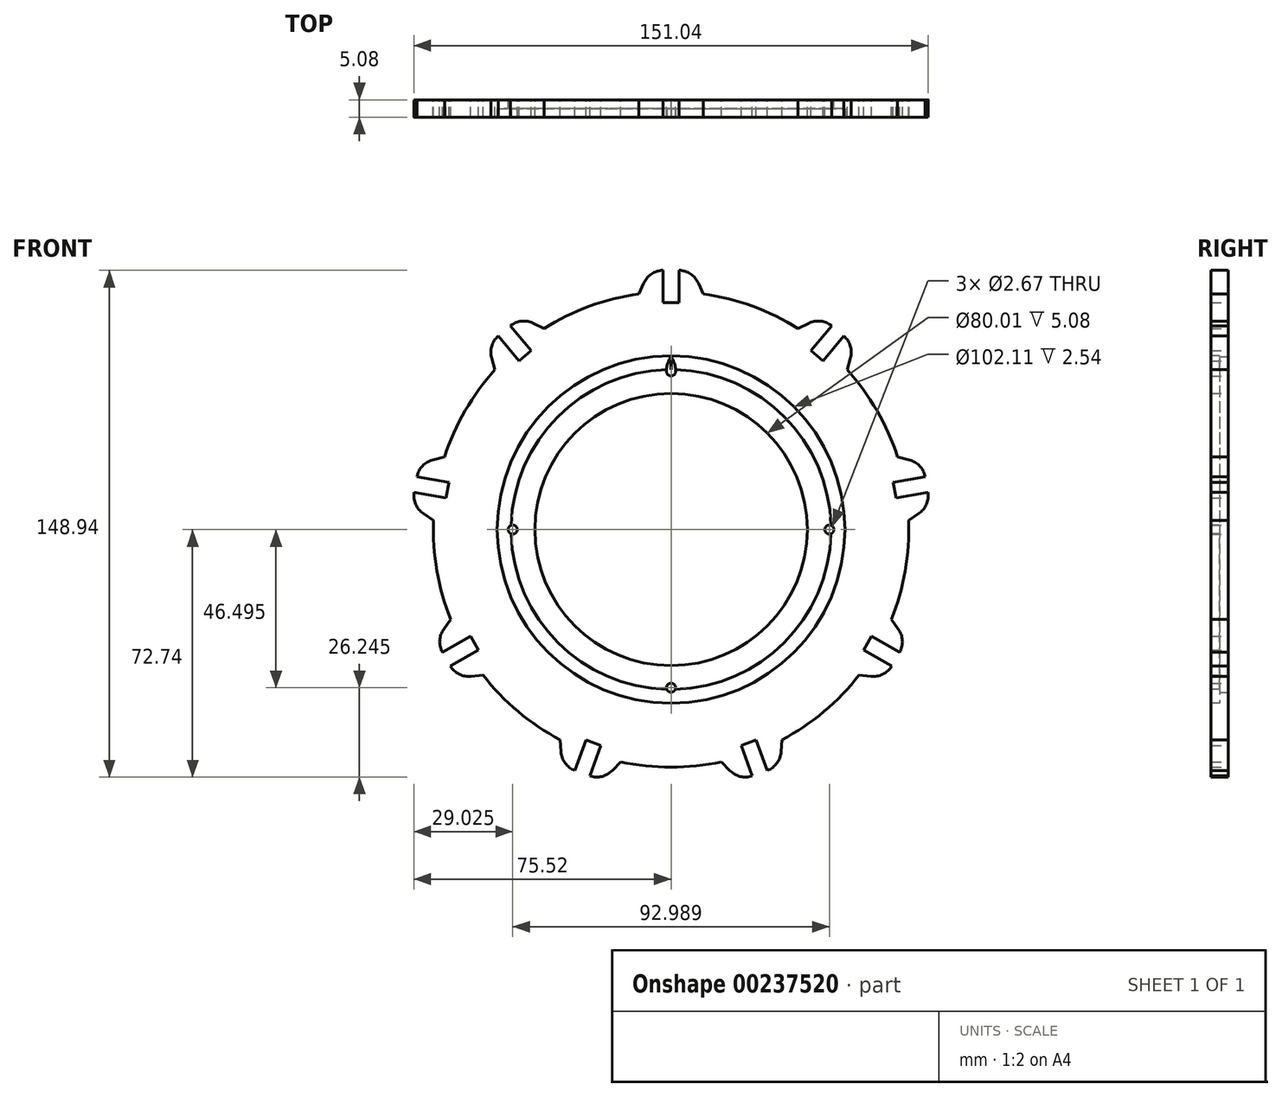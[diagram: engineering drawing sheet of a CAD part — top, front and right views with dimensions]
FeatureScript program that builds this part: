
annotation { "Feature Type Name" : "Feature", "Feature Type Description" : "" }
export const myFeature = defineFeature(function(context is Context, id is Id, definition is map)
    precondition{}
    {
        {
            var Q0;
            Q0=qCreatedBy(makeId("Front.planeOp"),FACE);
            var sketch = newSketch(context, id + "F0", { "sketchPlane" : qUnion([Q0])});
            skCircle(sketch, "E0", {"center": v(0, 0) * mm, "radius": 69.85 * mm});
            skCircle(sketch, "E1", {"center": v(0, 0) * mm, "radius": 40 * mm});
            skCircle(sketch, "E2", {"center": v(0, 0) * mm, "radius": 46.5 * mm, "construction": true});
            skPoint(sketch, "E3.center", {"position": v(0, -7.07) * mm});
            skLineSegment(sketch, "E4", {"start": v(-9.44, 69.2) * mm, "end": v(-8.02, 72.42) * mm});
            skLineSegment(sketch, "E5", {"start": v(-2.21, 76.2) * mm, "end": v(2.21, 76.2) * mm});
            skLineSegment(sketch, "E6", {"start": v(8.02, 72.42) * mm, "end": v(9.44, 69.2) * mm});
            skPoint(sketch, "E7", {"position": v(0, 76.2) * mm});
            skLineSegment(sketch, "E8", {"start": v(-9.44, 69.2) * mm, "end": v(-40, 0) * mm, "construction": true});
            skLineSegment(sketch, "E9", {"start": v(40, 0) * mm, "end": v(9.44, 69.2) * mm, "construction": true});
            skLineSegment(sketch, "E10", {"start": v(-2.35, 76.2) * mm, "end": v(-2.35, 66.67) * mm});
            skLineSegment(sketch, "E11", {"start": v(-2.35, 66.68) * mm, "end": v(2.35, 66.68) * mm});
            skLineSegment(sketch, "E12", {"start": v(2.35, 66.67) * mm, "end": v(2.35, 76.2) * mm});
            skPoint(sketch, "E13", {"position": v(0, 66.67) * mm});
            skPoint(sketch, "E14.visualSharp", {"position": v(-6.35, 76.2) * mm});
            skArc(sketch, "E14.filletArc", {"start": v(-2.21, 76.2) * mm, "mid": v(-5.68, 75.17) * mm, "end": v(-8.02, 72.42) * mm});
            skPoint(sketch, "E15.visualSharp", {"position": v(6.35, 76.2) * mm});
            skArc(sketch, "E15.filletArc", {"start": v(8.02, 72.42) * mm, "mid": v(5.68, 75.17) * mm, "end": v(2.21, 76.2) * mm});
            skCircle(sketch, "E16.MirrorC", {"center": v(0, 46.5) * mm, "radius": 1.33 * mm});
            skCircle(sketch, "E17", {"center": v(0, 0) * mm, "radius": 66.72 * mm, "construction": true});
            skCircle(sketch, "E18.1.0", {"center": v(-46.5, 0) * mm, "radius": 1.33 * mm});
            skCircle(sketch, "E18.2.0", {"center": v(0, -46.5) * mm, "radius": 1.33 * mm});
            skCircle(sketch, "E18.3.0", {"center": v(46.5, 0) * mm, "radius": 1.33 * mm});
            skCircle(sketch, "E19", {"center": v(0, 0) * mm, "radius": 50.8 * mm, "construction": true});
            skArc(sketch, "E20", {"start": v(1.33, 46.48) * mm, "mid": v(1, 48.74) * mm, "end": v(0, 50.8) * mm});
            skArc(sketch, "E21", {"start": v(0, 50.8) * mm, "mid": v(-1, 48.74) * mm, "end": v(-1.33, 46.48) * mm});
            skLineSegment(sketch, "E22.1.0", {"start": v(-51.72, 46.95) * mm, "end": v(-52.7, 50.32) * mm});
            skArc(sketch, "E22.1.1", {"start": v(-50.68, 56.95) * mm, "mid": v(-52.67, 53.93) * mm, "end": v(-52.7, 50.32) * mm});
            skLineSegment(sketch, "E22.1.2", {"start": v(-50.78, 56.86) * mm, "end": v(-44.66, 49.57) * mm});
            skLineSegment(sketch, "E22.1.3", {"start": v(-41.06, 52.59) * mm, "end": v(-47.18, 59.88) * mm});
            skArc(sketch, "E22.1.4", {"start": v(-40.4, 60.63) * mm, "mid": v(-43.97, 61.23) * mm, "end": v(-47.29, 59.8) * mm});
            skLineSegment(sketch, "E22.1.5", {"start": v(-40.4, 60.63) * mm, "end": v(-37.26, 59.08) * mm});
            skLineSegment(sketch, "E22.1.6", {"start": v(-44.66, 49.57) * mm, "end": v(-41.06, 52.59) * mm});
            skLineSegment(sketch, "E22.2.0", {"start": v(-69.8, 2.72) * mm, "end": v(-72.7, 4.68) * mm});
            skArc(sketch, "E22.2.1", {"start": v(-75.43, 11.05) * mm, "mid": v(-75.01, 7.46) * mm, "end": v(-72.7, 4.68) * mm});
            skLineSegment(sketch, "E22.2.2", {"start": v(-75.45, 10.92) * mm, "end": v(-66.07, 9.26) * mm});
            skLineSegment(sketch, "E22.2.3", {"start": v(-65.25, 13.9) * mm, "end": v(-74.63, 15.55) * mm});
            skArc(sketch, "E22.2.4", {"start": v(-69.92, 20.47) * mm, "mid": v(-73.04, 18.65) * mm, "end": v(-74.66, 15.41) * mm});
            skLineSegment(sketch, "E22.2.5", {"start": v(-69.92, 20.47) * mm, "end": v(-66.52, 21.31) * mm});
            skLineSegment(sketch, "E22.2.6", {"start": v(-66.07, 9.26) * mm, "end": v(-65.25, 13.9) * mm});
            skLineSegment(sketch, "E22.3.0", {"start": v(-55.22, -42.78) * mm, "end": v(-58.7, -43.15) * mm});
            skArc(sketch, "E22.3.1", {"start": v(-64.88, -40.02) * mm, "mid": v(-62.26, -42.5) * mm, "end": v(-58.7, -43.15) * mm});
            skLineSegment(sketch, "E22.3.2", {"start": v(-64.82, -40.13) * mm, "end": v(-56.57, -35.37) * mm});
            skLineSegment(sketch, "E22.3.3", {"start": v(-58.92, -31.3) * mm, "end": v(-67.17, -36.07) * mm});
            skArc(sketch, "E22.3.4", {"start": v(-66.72, -29.26) * mm, "mid": v(-67.94, -32.67) * mm, "end": v(-67.1, -36.18) * mm});
            skLineSegment(sketch, "E22.3.5", {"start": v(-66.72, -29.26) * mm, "end": v(-64.66, -26.43) * mm});
            skLineSegment(sketch, "E22.3.6", {"start": v(-56.57, -35.37) * mm, "end": v(-58.92, -31.3) * mm});
            skLineSegment(sketch, "E22.4.0", {"start": v(-14.8, -68.26) * mm, "end": v(-17.23, -70.8) * mm});
            skArc(sketch, "E22.4.1", {"start": v(-23.98, -72.36) * mm, "mid": v(-20.37, -72.58) * mm, "end": v(-17.23, -70.8) * mm});
            skLineSegment(sketch, "E22.4.2", {"start": v(-23.85, -72.4) * mm, "end": v(-20.6, -63.46) * mm});
            skLineSegment(sketch, "E22.4.3", {"start": v(-25.01, -61.85) * mm, "end": v(-28.27, -70.8) * mm});
            skArc(sketch, "E22.4.4", {"start": v(-32.3, -65.3) * mm, "mid": v(-31.05, -68.7) * mm, "end": v(-28.14, -70.85) * mm});
            skLineSegment(sketch, "E22.4.5", {"start": v(-32.3, -65.3) * mm, "end": v(-32.54, -61.8) * mm});
            skLineSegment(sketch, "E22.4.6", {"start": v(-20.6, -63.46) * mm, "end": v(-25.01, -61.85) * mm});
            skLineSegment(sketch, "E22.5.0", {"start": v(32.54, -61.8) * mm, "end": v(32.3, -65.3) * mm});
            skArc(sketch, "E22.5.1", {"start": v(28.14, -70.85) * mm, "mid": v(31.05, -68.7) * mm, "end": v(32.3, -65.3) * mm});
            skLineSegment(sketch, "E22.5.2", {"start": v(28.27, -70.8) * mm, "end": v(25.01, -61.85) * mm});
            skLineSegment(sketch, "E22.5.3", {"start": v(20.6, -63.46) * mm, "end": v(23.85, -72.4) * mm});
            skArc(sketch, "E22.5.4", {"start": v(17.23, -70.8) * mm, "mid": v(20.37, -72.58) * mm, "end": v(23.98, -72.36) * mm});
            skLineSegment(sketch, "E22.5.5", {"start": v(17.23, -70.8) * mm, "end": v(14.8, -68.26) * mm});
            skLineSegment(sketch, "E22.5.6", {"start": v(25.01, -61.85) * mm, "end": v(20.6, -63.46) * mm});
            skLineSegment(sketch, "E22.6.0", {"start": v(64.66, -26.43) * mm, "end": v(66.72, -29.26) * mm});
            skArc(sketch, "E22.6.1", {"start": v(67.1, -36.18) * mm, "mid": v(67.94, -32.67) * mm, "end": v(66.72, -29.26) * mm});
            skLineSegment(sketch, "E22.6.2", {"start": v(67.17, -36.07) * mm, "end": v(58.92, -31.3) * mm});
            skLineSegment(sketch, "E22.6.3", {"start": v(56.57, -35.37) * mm, "end": v(64.82, -40.13) * mm});
            skArc(sketch, "E22.6.4", {"start": v(58.7, -43.15) * mm, "mid": v(62.26, -42.5) * mm, "end": v(64.88, -40.02) * mm});
            skLineSegment(sketch, "E22.6.5", {"start": v(58.7, -43.15) * mm, "end": v(55.22, -42.78) * mm});
            skLineSegment(sketch, "E22.6.6", {"start": v(58.92, -31.3) * mm, "end": v(56.57, -35.37) * mm});
            skLineSegment(sketch, "E22.7.0", {"start": v(66.52, 21.31) * mm, "end": v(69.92, 20.47) * mm});
            skArc(sketch, "E22.7.1", {"start": v(74.66, 15.41) * mm, "mid": v(73.04, 18.65) * mm, "end": v(69.92, 20.47) * mm});
            skLineSegment(sketch, "E22.7.2", {"start": v(74.63, 15.55) * mm, "end": v(65.25, 13.9) * mm});
            skLineSegment(sketch, "E22.7.3", {"start": v(66.07, 9.26) * mm, "end": v(75.45, 10.92) * mm});
            skArc(sketch, "E22.7.4", {"start": v(72.7, 4.68) * mm, "mid": v(75.01, 7.46) * mm, "end": v(75.43, 11.05) * mm});
            skLineSegment(sketch, "E22.7.5", {"start": v(72.7, 4.68) * mm, "end": v(69.8, 2.72) * mm});
            skLineSegment(sketch, "E22.7.6", {"start": v(65.25, 13.9) * mm, "end": v(66.07, 9.26) * mm});
            skLineSegment(sketch, "E22.8.0", {"start": v(37.26, 59.08) * mm, "end": v(40.4, 60.63) * mm});
            skArc(sketch, "E22.8.1", {"start": v(47.29, 59.8) * mm, "mid": v(43.97, 61.23) * mm, "end": v(40.4, 60.63) * mm});
            skLineSegment(sketch, "E22.8.2", {"start": v(47.18, 59.88) * mm, "end": v(41.06, 52.59) * mm});
            skLineSegment(sketch, "E22.8.3", {"start": v(44.66, 49.57) * mm, "end": v(50.78, 56.86) * mm});
            skArc(sketch, "E22.8.4", {"start": v(52.7, 50.32) * mm, "mid": v(52.67, 53.93) * mm, "end": v(50.68, 56.95) * mm});
            skLineSegment(sketch, "E22.8.5", {"start": v(52.7, 50.32) * mm, "end": v(51.72, 46.95) * mm});
            skLineSegment(sketch, "E22.8.6", {"start": v(41.06, 52.59) * mm, "end": v(44.66, 49.57) * mm});
            skSolve(sketch);
        }
        {
            var Q0;
            Q0=makeQuery(id+"F0.imprint","IMPRINT",FACE,{"disambiguationData":[TD([[makeQuery(id+"F0.imprint","IMPRINT",EDGE,{"derivedFrom":sQuery(id+"F0.wireOp",EDGE,"E1")}),-1.0]])]});
            var Q1;
            {var subQ0=sQuery(id+"F0.wireOp",EDGE,"E22.1.5");Q1=makeQuery(id+"F0.imprint","IMPRINT",FACE,{"disambiguationData":[TD([[makeQuery(id+"F0.imprint","IMPRINT",EDGE,{"derivedFrom":subQ0}),-1.0]])]});}
            var Q2;
            {var subQ0=sQuery(id+"F0.wireOp",EDGE,"E22.1.0");Q2=makeQuery(id+"F0.imprint","IMPRINT",FACE,{"disambiguationData":[TD([[makeQuery(id+"F0.imprint","IMPRINT",EDGE,{"derivedFrom":subQ0}),-1.0]])]});}
            var Q3;
            {var subQ0=sQuery(id+"F0.wireOp",EDGE,"E4");Q3=makeQuery(id+"F0.imprint","IMPRINT",FACE,{"disambiguationData":[TD([[makeQuery(id+"F0.imprint","IMPRINT",EDGE,{"derivedFrom":subQ0}),-1.0]])]});}
            var Q4;
            {var subQ0=sQuery(id+"F0.wireOp",EDGE,"E6");Q4=makeQuery(id+"F0.imprint","IMPRINT",FACE,{"disambiguationData":[TD([[makeQuery(id+"F0.imprint","IMPRINT",EDGE,{"derivedFrom":subQ0}),-1.0]])]});}
            var Q5;
            {var subQ0=sQuery(id+"F0.wireOp",EDGE,"E22.8.0");Q5=makeQuery(id+"F0.imprint","IMPRINT",FACE,{"disambiguationData":[TD([[makeQuery(id+"F0.imprint","IMPRINT",EDGE,{"derivedFrom":subQ0}),-1.0]])]});}
            var Q6;
            {var subQ0=sQuery(id+"F0.wireOp",EDGE,"E22.8.5");Q6=makeQuery(id+"F0.imprint","IMPRINT",FACE,{"disambiguationData":[TD([[makeQuery(id+"F0.imprint","IMPRINT",EDGE,{"derivedFrom":subQ0}),-1.0]])]});}
            var Q7;
            {var subQ0=sQuery(id+"F0.wireOp",EDGE,"E22.7.0");Q7=makeQuery(id+"F0.imprint","IMPRINT",FACE,{"disambiguationData":[TD([[makeQuery(id+"F0.imprint","IMPRINT",EDGE,{"derivedFrom":subQ0}),-1.0]])]});}
            var Q8;
            {var subQ0=sQuery(id+"F0.wireOp",EDGE,"E22.7.5");Q8=makeQuery(id+"F0.imprint","IMPRINT",FACE,{"disambiguationData":[TD([[makeQuery(id+"F0.imprint","IMPRINT",EDGE,{"derivedFrom":subQ0}),-1.0]])]});}
            var Q9;
            {var subQ0=sQuery(id+"F0.wireOp",EDGE,"E22.6.0");Q9=makeQuery(id+"F0.imprint","IMPRINT",FACE,{"disambiguationData":[TD([[makeQuery(id+"F0.imprint","IMPRINT",EDGE,{"derivedFrom":subQ0}),-1.0]])]});}
            var Q10;
            {var subQ0=sQuery(id+"F0.wireOp",EDGE,"E22.6.5");Q10=makeQuery(id+"F0.imprint","IMPRINT",FACE,{"disambiguationData":[TD([[makeQuery(id+"F0.imprint","IMPRINT",EDGE,{"derivedFrom":subQ0}),-1.0]])]});}
            var Q11;
            {var subQ0=sQuery(id+"F0.wireOp",EDGE,"E22.5.5");Q11=makeQuery(id+"F0.imprint","IMPRINT",FACE,{"disambiguationData":[TD([[makeQuery(id+"F0.imprint","IMPRINT",EDGE,{"derivedFrom":subQ0}),-1.0]])]});}
            var Q12;
            {var subQ0=sQuery(id+"F0.wireOp",EDGE,"E22.5.0");Q12=makeQuery(id+"F0.imprint","IMPRINT",FACE,{"disambiguationData":[TD([[makeQuery(id+"F0.imprint","IMPRINT",EDGE,{"derivedFrom":subQ0}),-1.0]])]});}
            var Q13;
            {var subQ0=sQuery(id+"F0.wireOp",EDGE,"E22.4.5");Q13=makeQuery(id+"F0.imprint","IMPRINT",FACE,{"disambiguationData":[TD([[makeQuery(id+"F0.imprint","IMPRINT",EDGE,{"derivedFrom":subQ0}),-1.0]])]});}
            var Q14;
            {var subQ0=sQuery(id+"F0.wireOp",EDGE,"E22.4.0");Q14=makeQuery(id+"F0.imprint","IMPRINT",FACE,{"disambiguationData":[TD([[makeQuery(id+"F0.imprint","IMPRINT",EDGE,{"derivedFrom":subQ0}),-1.0]])]});}
            var Q15;
            {var subQ0=sQuery(id+"F0.wireOp",EDGE,"E22.3.0");Q15=makeQuery(id+"F0.imprint","IMPRINT",FACE,{"disambiguationData":[TD([[makeQuery(id+"F0.imprint","IMPRINT",EDGE,{"derivedFrom":subQ0}),-1.0]])]});}
            var Q16;
            {var subQ0=sQuery(id+"F0.wireOp",EDGE,"E22.3.5");Q16=makeQuery(id+"F0.imprint","IMPRINT",FACE,{"disambiguationData":[TD([[makeQuery(id+"F0.imprint","IMPRINT",EDGE,{"derivedFrom":subQ0}),-1.0]])]});}
            var Q17;
            {var subQ0=sQuery(id+"F0.wireOp",EDGE,"E22.2.0");Q17=makeQuery(id+"F0.imprint","IMPRINT",FACE,{"disambiguationData":[TD([[makeQuery(id+"F0.imprint","IMPRINT",EDGE,{"derivedFrom":subQ0}),-1.0]])]});}
            var Q18;
            {var subQ0=sQuery(id+"F0.wireOp",EDGE,"E22.2.5");Q18=makeQuery(id+"F0.imprint","IMPRINT",FACE,{"disambiguationData":[TD([[makeQuery(id+"F0.imprint","IMPRINT",EDGE,{"derivedFrom":subQ0}),-1.0]])]});}
            extrude(context, id + "F1", {"entities" : qUnion([Q0, Q1, Q2, Q3, Q4, Q5, Q6, Q7, Q8, Q9, Q10, Q11, Q12, Q13, Q14, Q15, Q16, Q17, Q18]), "depth" : 5.08 * mm});
        }
        {
            var Q0;
            Q0=makeQuery(id+"F1.opExtrude","CAP_FACE",FACE,{"disambiguationData":[OSD([sQuery(id+"F0.wireOp",EDGE,"E0"),sQuery(id+"F0.wireOp",EDGE,"E1"),sQuery(id+"F0.wireOp",EDGE,"s7rXqqL2-3z2l-88EV-UIsY-hwb08Po9ZJjJ"),sQuery(id+"F0.wireOp",EDGE,"E3.1.0"),sQuery(id+"F0.wireOp",EDGE,"E3.2.0"),sQuery(id+"F0.wireOp",EDGE,"E3.3.0"),sQuery(id+"F0.wireOp",EDGE,"E4"),sQuery(id+"F0.wireOp",EDGE,"E6"),sQuery(id+"F0.wireOp",EDGE,"E10"),sQuery(id+"F0.wireOp",EDGE,"E11"),sQuery(id+"F0.wireOp",EDGE,"E12"),sQuery(id+"F0.wireOp",EDGE,"E14.filletArc"),sQuery(id+"F0.wireOp",EDGE,"E15.filletArc"),sQuery(id+"F0.wireOp",EDGE,"e3144966-756d-47fd-8283-5f46bd2110e0.1.0"),sQuery(id+"F0.wireOp",EDGE,"e3144966-756d-47fd-8283-5f46bd2110e0.1.1"),sQuery(id+"F0.wireOp",EDGE,"e3144966-756d-47fd-8283-5f46bd2110e0.1.2"),sQuery(id+"F0.wireOp",EDGE,"e3144966-756d-47fd-8283-5f46bd2110e0.1.3"),sQuery(id+"F0.wireOp",EDGE,"e3144966-756d-47fd-8283-5f46bd2110e0.1.4"),sQuery(id+"F0.wireOp",EDGE,"e3144966-756d-47fd-8283-5f46bd2110e0.1.6"),sQuery(id+"F0.wireOp",EDGE,"e3144966-756d-47fd-8283-5f46bd2110e0.1.7"),sQuery(id+"F0.wireOp",EDGE,"e3144966-756d-47fd-8283-5f46bd2110e0.2.0"),sQuery(id+"F0.wireOp",EDGE,"e3144966-756d-47fd-8283-5f46bd2110e0.2.1"),sQuery(id+"F0.wireOp",EDGE,"e3144966-756d-47fd-8283-5f46bd2110e0.2.2"),sQuery(id+"F0.wireOp",EDGE,"e3144966-756d-47fd-8283-5f46bd2110e0.2.3"),sQuery(id+"F0.wireOp",EDGE,"e3144966-756d-47fd-8283-5f46bd2110e0.2.4"),sQuery(id+"F0.wireOp",EDGE,"e3144966-756d-47fd-8283-5f46bd2110e0.2.6"),sQuery(id+"F0.wireOp",EDGE,"e3144966-756d-47fd-8283-5f46bd2110e0.2.7"),sQuery(id+"F0.wireOp",EDGE,"e3144966-756d-47fd-8283-5f46bd2110e0.3.0"),sQuery(id+"F0.wireOp",EDGE,"e3144966-756d-47fd-8283-5f46bd2110e0.3.1"),sQuery(id+"F0.wireOp",EDGE,"e3144966-756d-47fd-8283-5f46bd2110e0.3.2"),sQuery(id+"F0.wireOp",EDGE,"e3144966-756d-47fd-8283-5f46bd2110e0.3.3"),sQuery(id+"F0.wireOp",EDGE,"e3144966-756d-47fd-8283-5f46bd2110e0.3.4"),sQuery(id+"F0.wireOp",EDGE,"e3144966-756d-47fd-8283-5f46bd2110e0.3.6"),sQuery(id+"F0.wireOp",EDGE,"e3144966-756d-47fd-8283-5f46bd2110e0.3.7"),sQuery(id+"F0.wireOp",EDGE,"e3144966-756d-47fd-8283-5f46bd2110e0.4.0"),sQuery(id+"F0.wireOp",EDGE,"e3144966-756d-47fd-8283-5f46bd2110e0.4.1"),sQuery(id+"F0.wireOp",EDGE,"e3144966-756d-47fd-8283-5f46bd2110e0.4.2"),sQuery(id+"F0.wireOp",EDGE,"e3144966-756d-47fd-8283-5f46bd2110e0.4.3"),sQuery(id+"F0.wireOp",EDGE,"e3144966-756d-47fd-8283-5f46bd2110e0.4.4"),sQuery(id+"F0.wireOp",EDGE,"e3144966-756d-47fd-8283-5f46bd2110e0.4.6"),sQuery(id+"F0.wireOp",EDGE,"e3144966-756d-47fd-8283-5f46bd2110e0.4.7"),sQuery(id+"F0.wireOp",EDGE,"e3144966-756d-47fd-8283-5f46bd2110e0.5.0"),sQuery(id+"F0.wireOp",EDGE,"e3144966-756d-47fd-8283-5f46bd2110e0.5.1"),sQuery(id+"F0.wireOp",EDGE,"e3144966-756d-47fd-8283-5f46bd2110e0.5.2"),sQuery(id+"F0.wireOp",EDGE,"e3144966-756d-47fd-8283-5f46bd2110e0.5.3"),sQuery(id+"F0.wireOp",EDGE,"e3144966-756d-47fd-8283-5f46bd2110e0.5.4"),sQuery(id+"F0.wireOp",EDGE,"e3144966-756d-47fd-8283-5f46bd2110e0.5.6"),sQuery(id+"F0.wireOp",EDGE,"e3144966-756d-47fd-8283-5f46bd2110e0.5.7"),sQuery(id+"F0.wireOp",EDGE,"e3144966-756d-47fd-8283-5f46bd2110e0.6.0"),sQuery(id+"F0.wireOp",EDGE,"e3144966-756d-47fd-8283-5f46bd2110e0.6.1"),sQuery(id+"F0.wireOp",EDGE,"e3144966-756d-47fd-8283-5f46bd2110e0.6.2"),sQuery(id+"F0.wireOp",EDGE,"e3144966-756d-47fd-8283-5f46bd2110e0.6.3"),sQuery(id+"F0.wireOp",EDGE,"e3144966-756d-47fd-8283-5f46bd2110e0.6.4"),sQuery(id+"F0.wireOp",EDGE,"e3144966-756d-47fd-8283-5f46bd2110e0.6.6"),sQuery(id+"F0.wireOp",EDGE,"e3144966-756d-47fd-8283-5f46bd2110e0.6.7"),sQuery(id+"F0.wireOp",EDGE,"e3144966-756d-47fd-8283-5f46bd2110e0.7.0"),sQuery(id+"F0.wireOp",EDGE,"e3144966-756d-47fd-8283-5f46bd2110e0.7.1"),sQuery(id+"F0.wireOp",EDGE,"e3144966-756d-47fd-8283-5f46bd2110e0.7.2"),sQuery(id+"F0.wireOp",EDGE,"e3144966-756d-47fd-8283-5f46bd2110e0.7.3"),sQuery(id+"F0.wireOp",EDGE,"e3144966-756d-47fd-8283-5f46bd2110e0.7.4"),sQuery(id+"F0.wireOp",EDGE,"e3144966-756d-47fd-8283-5f46bd2110e0.7.6"),sQuery(id+"F0.wireOp",EDGE,"e3144966-756d-47fd-8283-5f46bd2110e0.7.7"),sQuery(id+"F0.wireOp",EDGE,"e3144966-756d-47fd-8283-5f46bd2110e0.8.0"),sQuery(id+"F0.wireOp",EDGE,"e3144966-756d-47fd-8283-5f46bd2110e0.8.1"),sQuery(id+"F0.wireOp",EDGE,"e3144966-756d-47fd-8283-5f46bd2110e0.8.2"),sQuery(id+"F0.wireOp",EDGE,"e3144966-756d-47fd-8283-5f46bd2110e0.8.3"),sQuery(id+"F0.wireOp",EDGE,"e3144966-756d-47fd-8283-5f46bd2110e0.8.4"),sQuery(id+"F0.wireOp",EDGE,"e3144966-756d-47fd-8283-5f46bd2110e0.8.6"),sQuery(id+"F0.wireOp",EDGE,"e3144966-756d-47fd-8283-5f46bd2110e0.8.7")])],"isStart":false});
            var sketch = newSketch(context, id + "F2", { "sketchPlane" : qUnion([Q0])});
            skCircle(sketch, "E23", {"center": v(0, 0) * mm, "radius": 47 * mm});
            skCircle(sketch, "E24", {"center": v(0, 0) * mm, "radius": 51.05 * mm});
            skSolve(sketch);
        }
        {
            var Q0;
            Q0=makeQuery(id+"F2.imprint","IMPRINT",FACE,{"disambiguationData":[TD([[makeQuery(id+"F2.imprint","IMPRINT",EDGE,{"derivedFrom":sQuery(id+"F2.wireOp",EDGE,"E24")}),1.0]])]});
            var Q1;
            {var subQ0=sQuery(id+"F2.wireOp",EDGE,"E23");var subQ12=makeQuery(id+"F1.opExtrude","CAP_EDGE",EDGE,{"disambiguationData":[OSD([sQuery(id+"F0.wireOp",EDGE,"E20")])],"isStart":false});var subQ15=makeQuery(id+"F2.imprint","INTERSECT",VERTEX,{"derivedFrom":[subQ12,subQ0]});Q1=makeQuery(id+"F2.imprint","IMPRINT",FACE,{"disambiguationData":[TD([[makeQuery(id+"F2.imprint","IMPRINT",EDGE,{"disambiguationData":[TD([[subQ15,1.0]])],"derivedFrom":subQ0}),-1.0]])]});}
            extrude(context, id + "F3", {"entities" : qUnion([Q0, Q1]), "operationType" : NewBodyOperationType.REMOVE, "oppositeDirection" : true, "depth" : 2.54 * mm});
        }
        {
            var Q0;
            {var subQ0=sQuery(id+"F0.wireOp",EDGE,"E22.4.5");var subQ1=sQuery(id+"F0.wireOp",EDGE,"E22.3.6");var subQ2=sQuery(id+"F0.wireOp",EDGE,"E22.3.4");var subQ3=sQuery(id+"F0.wireOp",EDGE,"E22.4.2");var subQ4=sQuery(id+"F0.wireOp",EDGE,"E22.3.2");var subQ5=sQuery(id+"F0.wireOp",EDGE,"E22.4.4");var subQ6=sQuery(id+"F0.wireOp",EDGE,"E22.3.3");var subQ7=sQuery(id+"F0.wireOp",EDGE,"E22.3.1");var subQ8=sQuery(id+"F0.wireOp",EDGE,"E22.4.0");var subQ9=sQuery(id+"F0.wireOp",EDGE,"E22.2.6");var subQ10=sQuery(id+"F0.wireOp",EDGE,"E22.2.4");var subQ11=sQuery(id+"F0.wireOp",EDGE,"E22.2.2");var subQ12=sQuery(id+"F0.wireOp",EDGE,"E22.2.0");var subQ13=sQuery(id+"F0.wireOp",EDGE,"E22.1.2");var subQ14=sQuery(id+"F0.wireOp",EDGE,"E22.1.6");var subQ15=sQuery(id+"F0.wireOp",EDGE,"E22.5.0");var subQ16=sQuery(id+"F0.wireOp",EDGE,"E0");var subQ17=sQuery(id+"F0.wireOp",EDGE,"E22.6.5");var subQ18=sQuery(id+"F0.wireOp",EDGE,"E22.6.1");var subQ19=sQuery(id+"F0.wireOp",EDGE,"E12");var subQ20=sQuery(id+"F0.wireOp",EDGE,"E22.5.5");var subQ21=sQuery(id+"F0.wireOp",EDGE,"E22.3.0");var subQ22=sQuery(id+"F0.wireOp",EDGE,"E22.7.5");var subQ23=sQuery(id+"F0.wireOp",EDGE,"E22.3.5");var subQ24=sQuery(id+"F0.wireOp",EDGE,"E22.4.3");var subQ25=sQuery(id+"F0.wireOp",EDGE,"E22.8.5");var subQ26=sQuery(id+"F0.wireOp",EDGE,"E22.7.0");var subQ27=sQuery(id+"F0.wireOp",EDGE,"E22.1.1");var subQ28=sQuery(id+"F0.wireOp",EDGE,"E22.8.4");var subQ29=sQuery(id+"F0.wireOp",EDGE,"E14.filletArc");var subQ30=sQuery(id+"F0.wireOp",EDGE,"E22.6.0");var subQ31=sQuery(id+"F0.wireOp",EDGE,"E22.1.3");var subQ32=sQuery(id+"F0.wireOp",EDGE,"E22.8.6");var subQ33=sQuery(id+"F0.wireOp",EDGE,"E6");var subQ34=sQuery(id+"F0.wireOp",EDGE,"E22.8.0");var subQ35=sQuery(id+"F0.wireOp",EDGE,"E22.7.1");var subQ36=sQuery(id+"F0.wireOp",EDGE,"E4");var subQ37=sQuery(id+"F0.wireOp",EDGE,"E22.1.5");var subQ38=sQuery(id+"F0.wireOp",EDGE,"E22.6.4");var subQ39=sQuery(id+"F0.wireOp",EDGE,"E22.5.1");var subQ40=sQuery(id+"F0.wireOp",EDGE,"E22.4.6");var subQ41=sQuery(id+"F0.wireOp",EDGE,"E22.1.0");var subQ42=sQuery(id+"F0.wireOp",EDGE,"E22.2.5");var subQ43=sQuery(id+"F0.wireOp",EDGE,"E10");var subQ44=sQuery(id+"F0.wireOp",EDGE,"E22.6.6");var subQ45=sQuery(id+"F0.wireOp",EDGE,"E11");var subQ46=sQuery(id+"F0.wireOp",EDGE,"E15.filletArc");var subQ47=sQuery(id+"F0.wireOp",EDGE,"E22.2.3");var subQ48=sQuery(id+"F0.wireOp",EDGE,"E22.2.1");var subQ49=sQuery(id+"F0.wireOp",EDGE,"E22.4.1");var subQ50=sQuery(id+"F0.wireOp",EDGE,"E22.1.4");var subQ51=sQuery(id+"F0.wireOp",EDGE,"E22.5.2");var subQ52=sQuery(id+"F0.wireOp",EDGE,"E22.8.3");var subQ53=sQuery(id+"F0.wireOp",EDGE,"E22.5.3");var subQ54=sQuery(id+"F0.wireOp",EDGE,"E22.5.4");var subQ55=sQuery(id+"F0.wireOp",EDGE,"E22.5.6");var subQ56=sQuery(id+"F0.wireOp",EDGE,"E22.6.2");var subQ57=sQuery(id+"F0.wireOp",EDGE,"E22.6.3");var subQ58=sQuery(id+"F0.wireOp",EDGE,"E22.7.2");var subQ59=sQuery(id+"F0.wireOp",EDGE,"E22.7.3");var subQ60=sQuery(id+"F0.wireOp",EDGE,"E22.7.4");var subQ61=sQuery(id+"F0.wireOp",EDGE,"E22.7.6");var subQ62=sQuery(id+"F0.wireOp",EDGE,"E22.8.1");var subQ63=sQuery(id+"F0.wireOp",EDGE,"E22.8.2");Q0=makeQuery(id+"F3.boolean.opBoolean","SPLIT",FACE,{"disambiguationData":[TD([makeQuery(id+"F1.opExtrude","SWEPT_FACE",FACE,{"disambiguationData":[OSD([subQ36])]})])],"derivedFrom":makeQuery(id+"F1.opExtrude","CAP_FACE",FACE,{"disambiguationData":[OSD([subQ16,sQuery(id+"F0.wireOp",EDGE,"E1"),subQ36,subQ33,subQ43,subQ45,subQ19,subQ29,subQ46,sQuery(id+"F0.wireOp",EDGE,"E16.MirrorC"),sQuery(id+"F0.wireOp",EDGE,"E18.1.0"),sQuery(id+"F0.wireOp",EDGE,"E18.2.0"),sQuery(id+"F0.wireOp",EDGE,"E18.3.0"),sQuery(id+"F0.wireOp",EDGE,"E20"),sQuery(id+"F0.wireOp",EDGE,"E21"),subQ41,subQ27,subQ13,subQ31,subQ50,subQ37,subQ14,subQ12,subQ48,subQ11,subQ47,subQ10,subQ42,subQ9,subQ21,subQ7,subQ4,subQ6,subQ2,subQ23,subQ1,subQ8,subQ49,subQ3,subQ24,subQ5,subQ0,subQ40,subQ15,subQ39,subQ51,subQ53,subQ54,subQ20,subQ55,subQ30,subQ18,subQ56,subQ57,subQ38,subQ17,subQ44,subQ26,subQ35,subQ58,subQ59,subQ60,subQ22,subQ61,subQ34,subQ62,subQ63,subQ52,subQ28,subQ25,subQ32])],"isStart":false})});}
            var sketch = newSketch(context, id + "F4", { "sketchPlane" : qUnion([Q0])});
            skLineSegment(sketch, "E25", {"start": v(-0.03, 51.05) * mm, "end": v(-0.03, 46.99) * mm});
            skLineSegment(sketch, "E26", {"start": v(0.03, 51.05) * mm, "end": v(0.03, 46.99) * mm});
            skLineSegment(sketch, "E27", {"start": v(-0.03, 49.02) * mm, "end": v(0.03, 49.02) * mm, "construction": true});
            skPoint(sketch, "E28", {"position": v(0, 49.02) * mm});
            skArc(sketch, "E29", {"start": v(0.03, 51.05) * mm, "mid": v(0, 51.05) * mm, "end": v(-0.03, 51.05) * mm});
            skArc(sketch, "E30", {"start": v(0.03, 46.99) * mm, "mid": v(0, 46.99) * mm, "end": v(-0.03, 46.99) * mm});
            skSolve(sketch);
        }
        {
            var Q0;
            Q0=qSketchRegion(id+"F4",true);
            var Q1;
            Q1=makeQuery(id+"F3.boolean.opBoolean","COPY",FACE,{"derivedFrom":makeQuery(id+"F3.opExtrude","CAP_FACE",FACE,{"disambiguationData":[OSD([sQuery(id+"F0.wireOp",EDGE,"E18.1.0"),sQuery(id+"F0.wireOp",EDGE,"E18.2.0"),sQuery(id+"F0.wireOp",EDGE,"E18.3.0"),sQuery(id+"F0.wireOp",EDGE,"E20"),sQuery(id+"F0.wireOp",EDGE,"E21"),sQuery(id+"F2.wireOp",EDGE,"E23"),sQuery(id+"F2.wireOp",EDGE,"E24")])],"isStart":false})});
            extrude(context, id + "F5", {"entities" : qUnion([Q0]), "operationType" : NewBodyOperationType.ADD, "endBound" : BoundingType.UP_TO_SURFACE, "oppositeDirection" : true, "endBoundEntityFace" : qUnion([Q1]), "depth" : 25.4 * mm});
        }
    });
